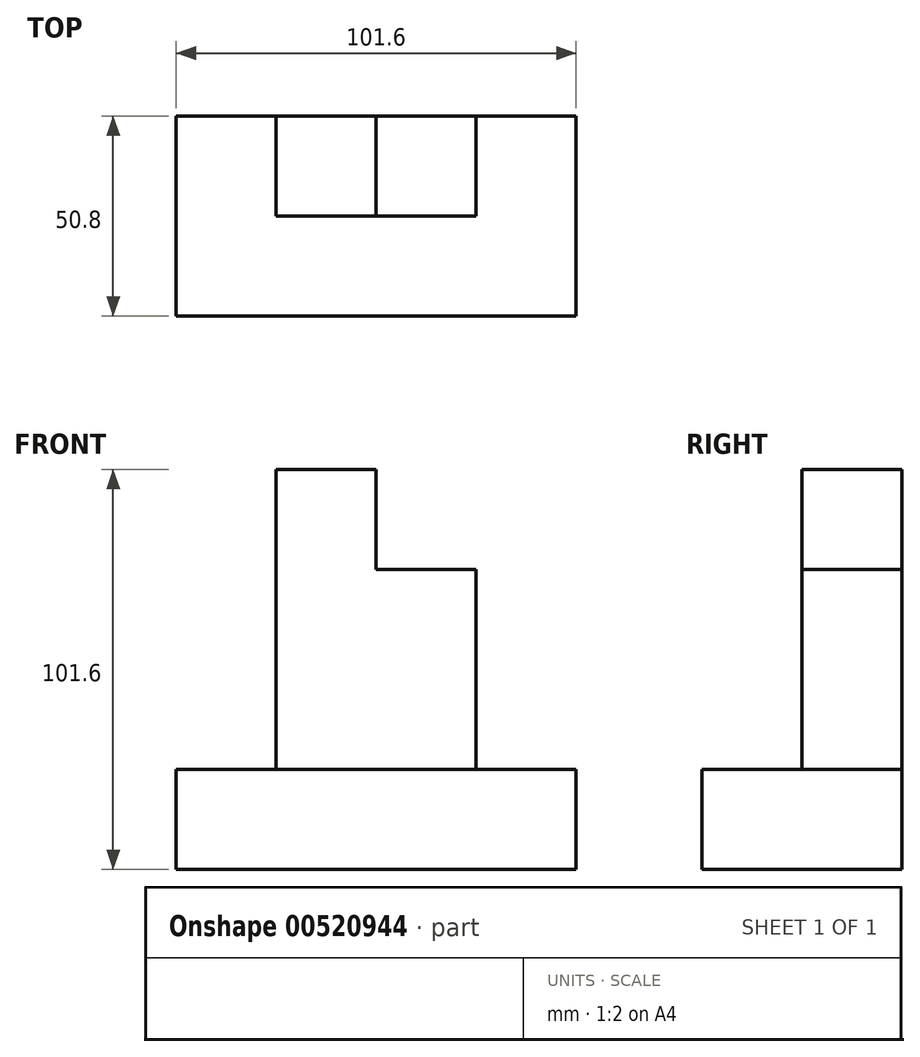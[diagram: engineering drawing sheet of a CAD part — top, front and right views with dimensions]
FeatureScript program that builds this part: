
annotation { "Feature Type Name" : "Feature", "Feature Type Description" : "" }
export const myFeature = defineFeature(function(context is Context, id is Id, definition is map)
    precondition{}
    {
        {
            var Q0;
            Q0=qCreatedBy(makeId("Top.planeOp"),FACE);
            var sketch = newSketch(context, id + "F0", { "sketchPlane" : qUnion([Q0])});
            skLineSegment(sketch, "E0.bottom", {"start": v(0, 0) * mm, "end": v(101.6, 0) * mm});
            skLineSegment(sketch, "E0.top", {"start": v(0, -50.8) * mm, "end": v(101.6, -50.8) * mm});
            skLineSegment(sketch, "E0.left", {"start": v(0, 0) * mm, "end": v(0, -50.8) * mm});
            skLineSegment(sketch, "E0.right", {"start": v(101.6, 0) * mm, "end": v(101.6, -50.8) * mm});
            skSolve(sketch);
        }
        {
            var Q0;
            Q0 = qSketchRegion(id + "F0", true);
            extrude(context, id + "F1", {"entities" : qUnion([Q0]), "depth" : 25.4 * mm, "offsetDistance" : 25.4 * mm});
        }
        {
            var Q0;
            Q0=makeQuery(id+"F1.opExtrude","CAP_FACE",FACE,{"disambiguationData":[OSD([sQuery(id+"F0.wireOp",EDGE,"E0.bottom"),sQuery(id+"F0.wireOp",EDGE,"E0.top"),sQuery(id+"F0.wireOp",EDGE,"E0.left"),sQuery(id+"F0.wireOp",EDGE,"E0.right")])],"isStart":false});
            var sketch = newSketch(context, id + "F2", { "sketchPlane" : qUnion([Q0])});
            skLineSegment(sketch, "E1.bottom", {"start": v(25.4, -25.4) * mm, "end": v(76.2, -25.4) * mm});
            skLineSegment(sketch, "E1.top", {"start": v(25.4, 0) * mm, "end": v(76.2, 0) * mm});
            skLineSegment(sketch, "E1.left", {"start": v(25.4, -25.4) * mm, "end": v(25.4, 0) * mm});
            skLineSegment(sketch, "E1.right", {"start": v(76.2, -25.4) * mm, "end": v(76.2, 0) * mm});
            skSolve(sketch);
        }
        {
            var Q0;
            Q0 = qSketchRegion(id + "F2", true);
            extrude(context, id + "F3", {"entities" : qUnion([Q0]), "operationType" : NewBodyOperationType.ADD, "depth" : 50.8 * mm, "offsetDistance" : 25.4 * mm});
        }
        {
            var Q0;
            Q0=makeQuery(id+"F3.opExtrude","CAP_FACE",FACE,{"disambiguationData":[OSD([sQuery(id+"F2.wireOp",EDGE,"E1.bottom"),sQuery(id+"F2.wireOp",EDGE,"E1.top"),sQuery(id+"F2.wireOp",EDGE,"E1.left"),sQuery(id+"F2.wireOp",EDGE,"E1.right")])],"isStart":false});
            var sketch = newSketch(context, id + "F4", { "sketchPlane" : qUnion([Q0])});
            skLineSegment(sketch, "E2.bottom", {"start": v(25.4, 0) * mm, "end": v(50.8, 0) * mm});
            skLineSegment(sketch, "E2.top", {"start": v(25.4, -25.4) * mm, "end": v(50.8, -25.4) * mm});
            skLineSegment(sketch, "E2.left", {"start": v(25.4, 0) * mm, "end": v(25.4, -25.4) * mm});
            skLineSegment(sketch, "E2.right", {"start": v(50.8, 0) * mm, "end": v(50.8, -25.4) * mm});
            skSolve(sketch);
        }
        {
            var Q0;
            Q0=makeQuery(id+"F4.imprint","IMPRINT",FACE,{"disambiguationData":[TD([[makeQuery(id+"F4.imprint","IMPRINT",EDGE,{"derivedFrom":sQuery(id+"F4.wireOp",EDGE,"E2.bottom")}),-1.0]])]});
            extrude(context, id + "F5", {"entities" : qUnion([Q0]), "operationType" : NewBodyOperationType.ADD, "depth" : 25.4 * mm, "offsetDistance" : 25.4 * mm});
        }
    });
